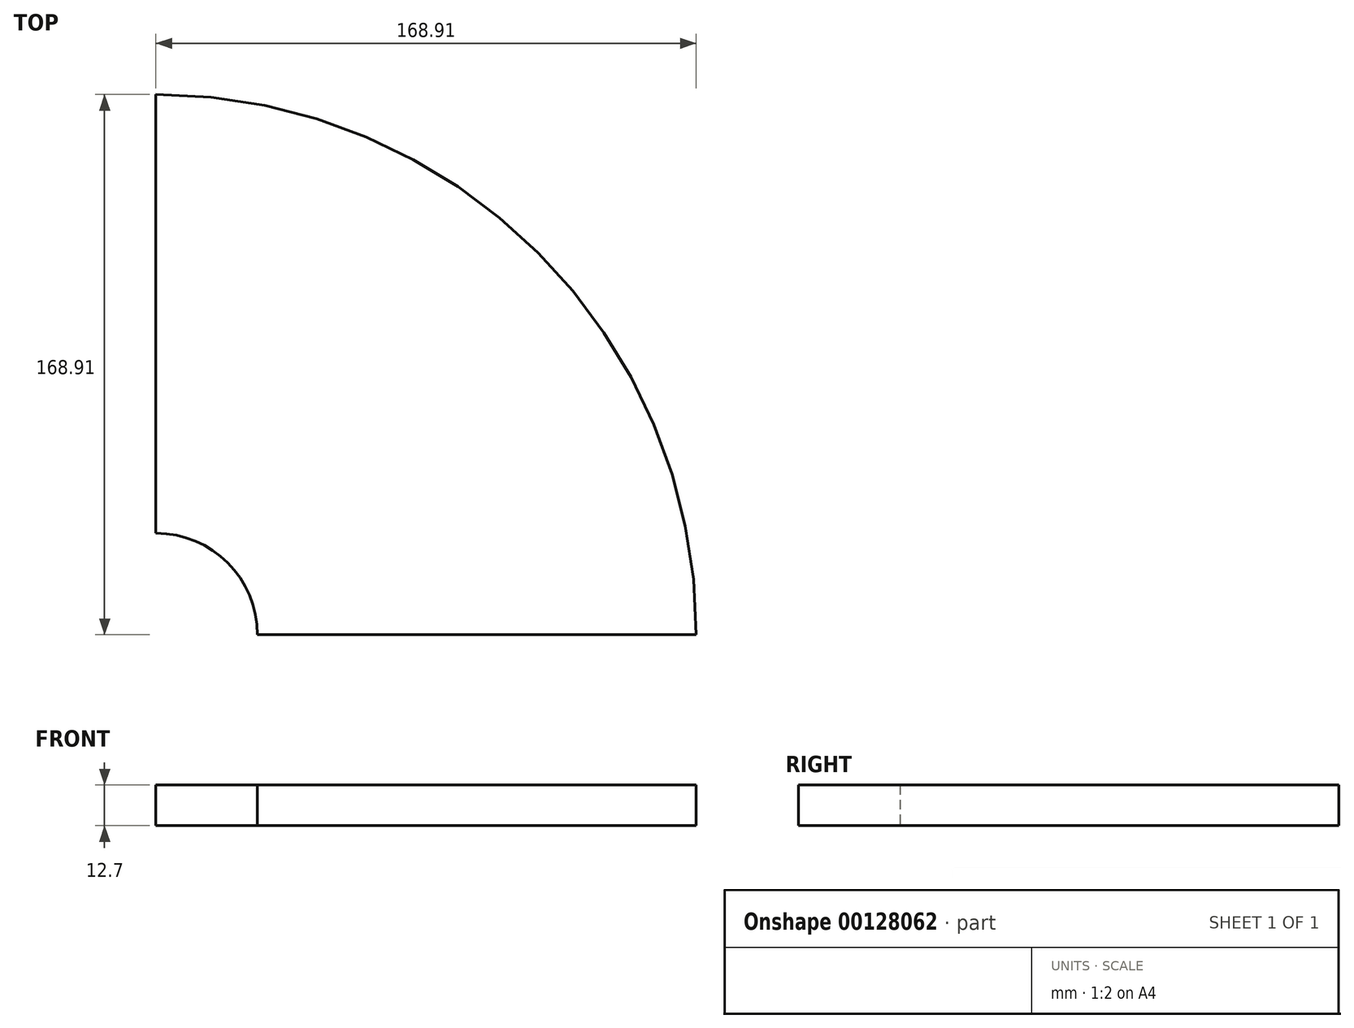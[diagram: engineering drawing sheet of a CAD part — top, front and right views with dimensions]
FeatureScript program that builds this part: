
annotation { "Feature Type Name" : "Feature", "Feature Type Description" : "" }
export const myFeature = defineFeature(function(context is Context, id is Id, definition is map)
    precondition{}
    {
        {
            var Q0;
            Q0=qCreatedBy(makeId("Top.planeOp"),FACE);
            var sketch = newSketch(context, id + "F0", { "sketchPlane" : qUnion([Q0])});
            skArc(sketch, "E0", {"start": v(31.75, 0) * mm, "mid": v(22.45, 22.45) * mm, "end": v(0, 31.75) * mm});
            skArc(sketch, "E1", {"start": v(168.91, 0) * mm, "mid": v(119.44, 119.44) * mm, "end": v(0, 168.91) * mm});
            skLineSegment(sketch, "E2", {"start": v(31.75, 0) * mm, "end": v(168.91, 0) * mm});
            skLineSegment(sketch, "E3", {"start": v(0, 168.91) * mm, "end": v(0, 31.75) * mm});
            skSolve(sketch);
        }
        {
            var Q0;
            Q0=makeQuery(id+"F0.imprint","IMPRINT",FACE,{"disambiguationData":[TD([[makeQuery(id+"F0.imprint","IMPRINT",EDGE,{"derivedFrom":sQuery(id+"F0.wireOp",EDGE,"E0")}),-1.0]])]});
            extrude(context, id + "F1", {"entities" : qUnion([Q0]), "depth" : 12.7 * mm});
        }
    });
